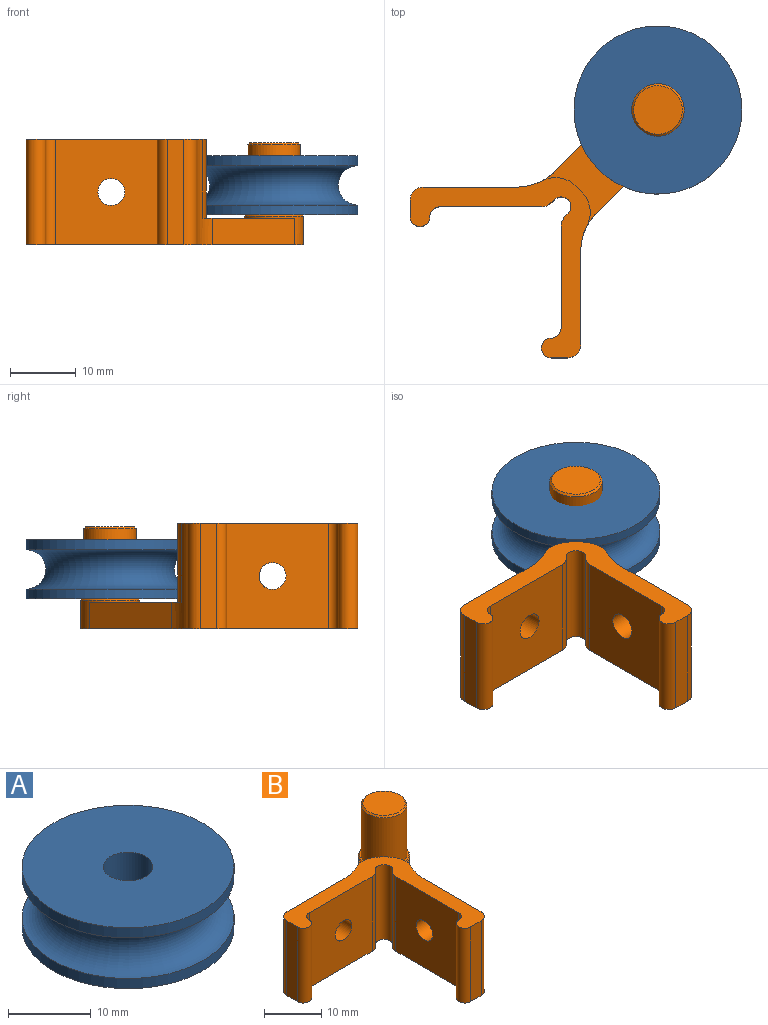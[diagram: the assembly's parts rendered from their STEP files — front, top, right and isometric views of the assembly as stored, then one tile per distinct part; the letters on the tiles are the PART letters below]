
ASSEMBLY  parts=2 mates=1
PART A: 6 faces, bbox 32.3x32.3x9 mm
  f0: torus R=12.8mm, axis (0,0,1), area 644.9mm2, adj f1,f5
  f1: cylinder r=12.8mm len=25.6mm, axis (0,0,1), area 120.6mm2, adj f0,f2
  f2: plane 25.6x25.6mm, normal (0,0,-1), area 486.4mm2, adj f1,f3
  f3: cylinder r=3mm len=9mm, axis (0,0,1), area 169.6mm2, adj f2,f4
  f4: plane 25.6x25.6mm, normal (0,0,1), area 486.4mm2, adj f3,f5
  f5: cylinder r=12.8mm len=25.6mm, axis (0,0,1), area 120.6mm2, adj f0,f4
PART B: 35 faces, bbox 42.2x42.2x16 mm
  f0: cylinder r=1.5mm len=16mm, axis (0,0,-1), area 37.7mm2, adj f1,f21,f23,f32
  f1: plane 16x15.55mm, normal (0,-1,0), area 235.6mm2, adj f0,f2,f23,f32,f33
  f2: cylinder r=2mm len=16mm, axis (0,0,-1), area 25.1mm2, adj f1,f3,f23,f32
  f3: plane 16x0.48mm, normal (0.71,-0.71,0), area 10.7mm2, adj f2,f4,f23,f32
  f4: cylinder r=1.5mm len=16mm, axis (0,0,-1), area 75.4mm2, adj f3,f5,f23,f32
  f5: plane 16x0.48mm, normal (-0.71,0.71,0), area 10.7mm2, adj f4,f6,f23,f32
  f6: cylinder r=2mm len=16mm, axis (0,0,-1), area 25.1mm2, adj f5,f7,f23,f32
  f7: plane 16x15.55mm, normal (-1,0,0), area 235.6mm2, adj f6,f8,f23,f32,f34
  f8: cylinder r=1.5mm len=16mm, axis (0,0,-1), area 37.7mm2, adj f7,f9,f23,f32
  f9: cylinder r=1.5mm len=16mm, axis (0,0,-1), area 75.4mm2, adj f8,f10,f23,f32
  f10: plane 16x2.5mm, normal (0,-1,0), area 40mm2, adj f9,f11,f23,f32
  f11: cylinder r=2mm len=16mm, axis (0,0,-1), area 50.3mm2, adj f10,f12,f23,f32
  f12: plane 16x14.32mm, normal (1,0,0), area 216mm2, adj f11,f13,f23,f32,f34
  f13: cylinder r=8mm len=16mm, axis (0,0,-1), area 71.7mm2, adj f12,f14,f22,f23,f29,f32
  f14: plane 12.59x12.59mm, normal (0.71,-0.71,0), area 71.2mm2, adj f13,f15,f22,f23
  f15: cylinder r=4.5mm len=9mm, axis (0,0,-1), area 65mm2, adj f14,f16,f22,f23,f25
  f16: plane 12.59x12.59mm, normal (-0.71,0.71,0), area 71.2mm2, adj f15,f17,f22,f23
  f17: cylinder r=8mm len=16mm, axis (0,0,-1), area 71.7mm2, adj f16,f18,f22,f23,f31,f32
  f18: plane 16x14.32mm, normal (0,1,0), area 216mm2, adj f17,f19,f23,f32,f33
  f19: cylinder r=2mm len=16mm, axis (0,0,-1), area 50.3mm2, adj f18,f20,f23,f32
  f20: plane 16x2.5mm, normal (-1,0,0), area 40mm2, adj f19,f21,f23,f32
  f21: cylinder r=1.5mm len=16mm, axis (0,0,-1), area 75.4mm2, adj f0,f20,f23,f32
  f22: plane 20.88x20.88mm, normal (0,0,1), area 126.7mm2, adj f13,f14,f15,f16,f17,f29,f30,f31
  f23: plane 42.25x42.25mm, normal (0,0,-1), area 360.7mm2, adj f0,f1,f2,f3,f4,f5,f6,f7
  f24: plane 8.6x8.6mm, normal (0,0,1), area 7.8mm2, adj f25,f26
  f25: cone r=4.3mm half-angle=45deg, axis (0,0,-1), area 7.8mm2, adj f15,f24
  f26: cylinder r=4mm len=10.7mm, axis (0,0,-1), area 268.9mm2, adj f24,f28
  f27: plane 7.4x7.4mm, normal (0,0,1), area 43mm2, adj f28
  f28: cone r=3.7mm half-angle=45deg, axis (0,0,-1), area 10.3mm2, adj f26,f27
  f29: cylinder r=4.5mm len=12mm, axis (0,0,-1), area 68.7mm2, adj f13,f22,f30,f32
  f30: plane 12x0.79mm, normal (0.71,0.71,0), area 13.4mm2, adj f22,f29,f31,f32
  f31: cylinder r=4.5mm len=12mm, axis (0,0,-1), area 68.7mm2, adj f17,f22,f30,f32
  f32: plane 27.44x27.44mm, normal (0,0,1), area 170.4mm2, adj f0,f1,f2,f3,f4,f5,f6,f7
  f33: cylinder r=2.05mm len=4.1mm, axis (0,1,0), area 38.6mm2, adj f1,f18
  f34: cylinder r=2.05mm len=4.1mm, axis (1,0,0), area 38.6mm2, adj f7,f12
PLACE A t=(2.96,38.67,13.88)mm
PLACE B t=(-21.79,13.92,4.88)mm
MATE fastened A.f0 <-> B.f15  axis (0,0,-1) through (2.96,38.67,9.38)mm
